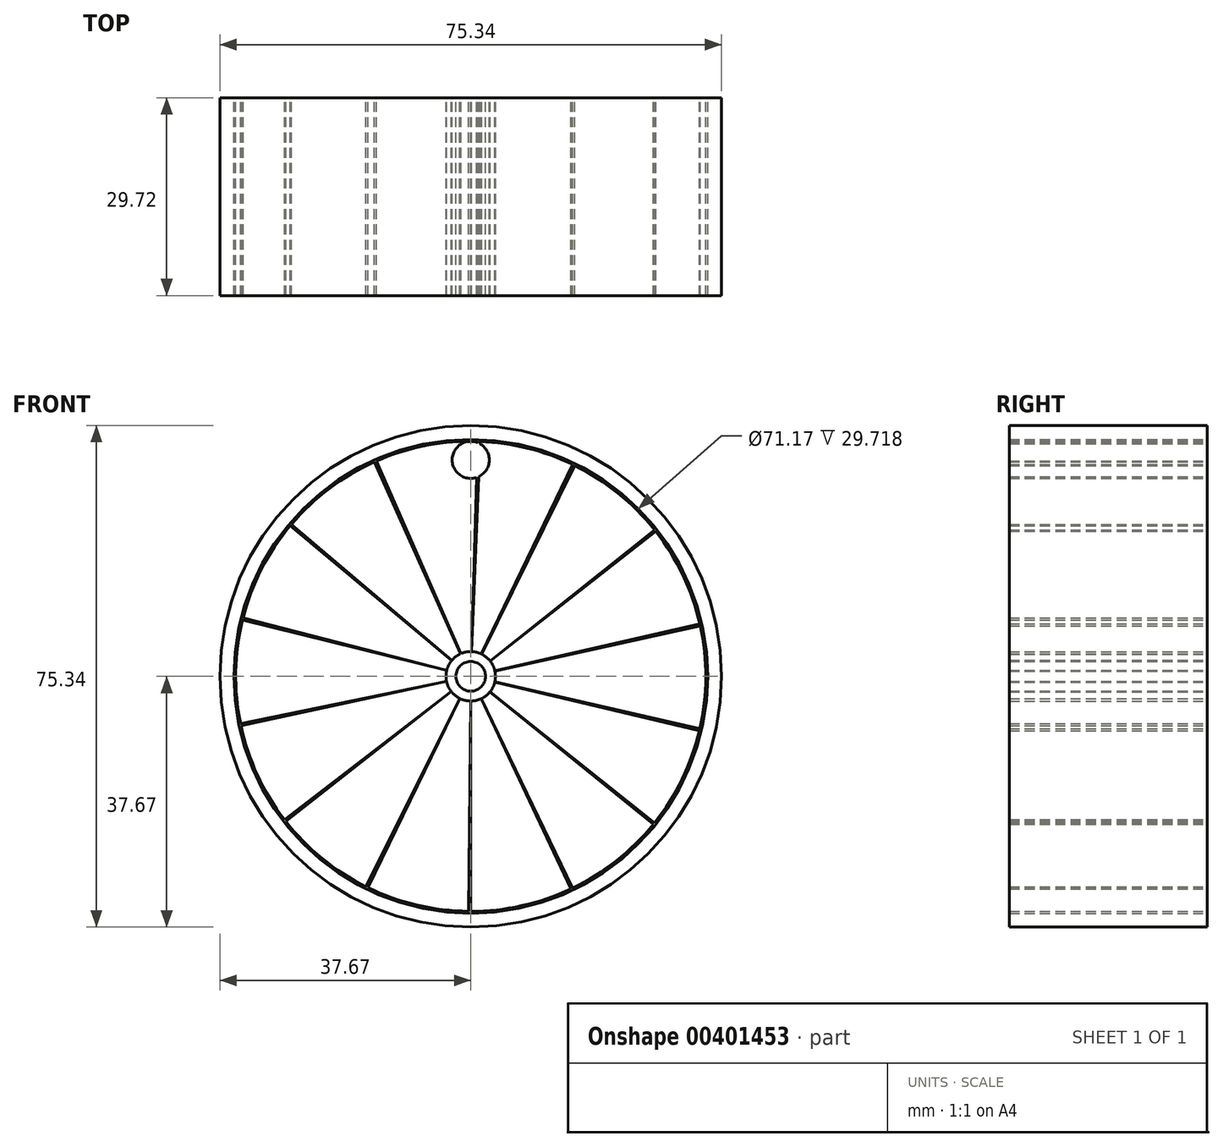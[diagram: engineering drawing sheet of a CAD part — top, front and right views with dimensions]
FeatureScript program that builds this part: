
annotation { "Feature Type Name" : "Feature", "Feature Type Description" : "" }
export const myFeature = defineFeature(function(context is Context, id is Id, definition is map)
    precondition{}
    {
        {
            var Q0;
            Q0=qCreatedBy(makeId("Front.planeOp"),FACE);
            var sketch = newSketch(context, id + "F0", { "sketchPlane" : qUnion([Q0])});
            skLineSegment(sketch, "E0", {"start": v(-30.16, 0) * mm, "end": v(30.16, 0) * mm, "construction": true});
            skCircle(sketch, "E1", {"center": v(0, 0) * mm, "radius": 30.16 * mm});
            skPoint(sketch, "E2.middle", {"position": v(0, 30.16) * mm});
            skCircle(sketch, "E3", {"center": v(0, 0) * mm, "radius": 1.9 * mm});
            skCircle(sketch, "E4", {"center": v(0, 0) * mm, "radius": 3.18 * mm});
            skCircle(sketch, "E5.0", {"center": v(0, 0) * mm, "radius": 2.54 * mm, "construction": true});
            skLineSegment(sketch, "E6.1.0", {"start": v(13.09, 27.18) * mm, "end": v(1.1, 2.29) * mm});
            skLineSegment(sketch, "E6.2.0", {"start": v(23.58, 18.8) * mm, "end": v(1.99, 1.58) * mm});
            skLineSegment(sketch, "E6.3.0", {"start": v(29.4, 6.71) * mm, "end": v(2.48, 0.57) * mm});
            skLineSegment(sketch, "E6.4.0", {"start": v(29.4, -6.71) * mm, "end": v(2.48, -0.57) * mm});
            skLineSegment(sketch, "E6.5.0", {"start": v(23.58, -18.8) * mm, "end": v(1.99, -1.58) * mm});
            skLineSegment(sketch, "E6.6.0", {"start": v(13.09, -27.18) * mm, "end": v(1.1, -2.29) * mm});
            skLineSegment(sketch, "E6.7.0", {"start": v(0, -30.16) * mm, "end": v(0, -2.54) * mm});
            skLineSegment(sketch, "E6.anchor1", {"start": v(0, 0) * mm, "end": v(0, 2.54) * mm, "construction": true});
            skLineSegment(sketch, "E6.anchor2", {"start": v(0, 0) * mm, "end": v(0, -2.54) * mm, "construction": true});
            skLineSegment(sketch, "E7.1.0", {"start": v(-13.2, -27.12) * mm, "end": v(-1.11, -2.28) * mm});
            skLineSegment(sketch, "E7.2.0", {"start": v(-23.75, -18.6) * mm, "end": v(-2, -1.57) * mm});
            skLineSegment(sketch, "E7.3.0", {"start": v(-29.5, -6.33) * mm, "end": v(-2.48, -0.53) * mm});
            skLineSegment(sketch, "E7.4.0", {"start": v(-29.28, 7.22) * mm, "end": v(-2.47, 0.6) * mm});
            skLineSegment(sketch, "E7.5.0", {"start": v(-23.17, 19.32) * mm, "end": v(-1.95, 1.63) * mm});
            skLineSegment(sketch, "E7.6.0", {"start": v(-12.37, 27.5) * mm, "end": v(-1.04, 2.32) * mm});
            skLineSegment(sketch, "E7.7.0", {"start": v(0.92, 30.15) * mm, "end": v(0.08, 2.54) * mm});
            skLineSegment(sketch, "E8.1.0", {"start": v(1.18, 30.14) * mm, "end": v(0.1, 2.54) * mm});
            skLineSegment(sketch, "E8.1.1", {"start": v(13.32, 27.06) * mm, "end": v(1.12, 2.28) * mm});
            skLineSegment(sketch, "E8.1.2", {"start": v(23.75, 18.6) * mm, "end": v(2, 1.57) * mm});
            skLineSegment(sketch, "E8.1.3", {"start": v(29.46, 6.45) * mm, "end": v(2.48, 0.54) * mm});
            skLineSegment(sketch, "E8.1.4", {"start": v(29.35, -6.97) * mm, "end": v(2.47, -0.59) * mm});
            skLineSegment(sketch, "E8.1.5", {"start": v(23.42, -19.01) * mm, "end": v(1.97, -1.6) * mm});
            skLineSegment(sketch, "E8.1.6", {"start": v(12.85, -27.29) * mm, "end": v(1.08, -2.3) * mm});
            skLineSegment(sketch, "E8.1.7", {"start": v(-0.26, -30.16) * mm, "end": v(-0.02, -2.54) * mm});
            skLineSegment(sketch, "E8.1.8", {"start": v(-13.44, -27) * mm, "end": v(-1.13, -2.27) * mm});
            skLineSegment(sketch, "E8.1.9", {"start": v(-29.55, -6.07) * mm, "end": v(-2.49, -0.51) * mm});
            skLineSegment(sketch, "E8.1.10", {"start": v(-29.22, 7.48) * mm, "end": v(-2.46, 0.63) * mm});
            skLineSegment(sketch, "E8.1.11", {"start": v(-23.9, -18.4) * mm, "end": v(-2.01, -1.55) * mm});
            skLineSegment(sketch, "E8.1.12", {"start": v(-23, 19.52) * mm, "end": v(-1.94, 1.64) * mm});
            skLineSegment(sketch, "E8.1.13", {"start": v(-12.13, 27.62) * mm, "end": v(-1.02, 2.33) * mm});
            skLineSegment(sketch, "E8.anchor1", {"start": v(0, 0) * mm, "end": v(-23.75, -18.6) * mm, "construction": true});
            skLineSegment(sketch, "E8.anchor2", {"start": v(0, 0) * mm, "end": v(-23.9, -18.4) * mm, "construction": true});
            skCircle(sketch, "E9.0", {"center": v(0, 0) * mm, "radius": 3.05 * mm});
            skCircle(sketch, "E10.0", {"center": v(0, 0) * mm, "radius": 2.03 * mm});
            skCircle(sketch, "E11.0", {"center": v(0, 0) * mm, "radius": 32.2 * mm});
            skCircle(sketch, "E12.0", {"center": v(0, 0) * mm, "radius": 30.42 * mm});
            skCircle(sketch, "E13", {"center": v(0, 27.78) * mm, "radius": 2.38 * mm});
            skSolve(sketch);
        }
        {
            var Q0;
            Q0=makeQuery(id+"F0.imprint","IMPRINT",FACE,{"disambiguationData":[TD([[makeQuery(id+"F0.imprint","IMPRINT",EDGE,{"derivedFrom":sQuery(id+"F0.wireOp",EDGE,"E11.0")}),1.0]])]});
            var Q1;
            {var subQ0=sQuery(id+"F0.wireOp",EDGE,"E6.2.0");var subQ1=sQuery(id+"F0.wireOp",EDGE,"E1");var subQ2=makeQuery(id+"F0.imprint","INTERSECT",VERTEX,{"derivedFrom":[subQ1,subQ0]});Q1=makeQuery(id+"F0.imprint","IMPRINT",FACE,{"disambiguationData":[TD([[makeQuery(id+"F0.imprint","IMPRINT",EDGE,{"disambiguationData":[TD([[subQ2,-1.0]])],"derivedFrom":subQ1}),1.0]])]});}
            var Q2;
            {var subQ0=sQuery(id+"F0.wireOp",EDGE,"E6.3.0");var subQ1=sQuery(id+"F0.wireOp",EDGE,"E1");var subQ2=makeQuery(id+"F0.imprint","INTERSECT",VERTEX,{"derivedFrom":[subQ1,subQ0]});Q2=makeQuery(id+"F0.imprint","IMPRINT",FACE,{"disambiguationData":[TD([[makeQuery(id+"F0.imprint","IMPRINT",EDGE,{"disambiguationData":[TD([[subQ2,-1.0]])],"derivedFrom":subQ1}),1.0]])]});}
            var Q3;
            {var subQ0=sQuery(id+"F0.wireOp",EDGE,"E6.4.0");var subQ1=sQuery(id+"F0.wireOp",EDGE,"E1");var subQ2=makeQuery(id+"F0.imprint","INTERSECT",VERTEX,{"derivedFrom":[subQ1,subQ0]});Q3=makeQuery(id+"F0.imprint","IMPRINT",FACE,{"disambiguationData":[TD([[makeQuery(id+"F0.imprint","IMPRINT",EDGE,{"disambiguationData":[TD([[subQ2,-1.0]])],"derivedFrom":subQ1}),1.0]])]});}
            var Q4;
            {var subQ0=sQuery(id+"F0.wireOp",EDGE,"E6.6.0");var subQ1=sQuery(id+"F0.wireOp",EDGE,"E1");var subQ2=makeQuery(id+"F0.imprint","INTERSECT",VERTEX,{"derivedFrom":[subQ1,subQ0]});Q4=makeQuery(id+"F0.imprint","IMPRINT",FACE,{"disambiguationData":[TD([[makeQuery(id+"F0.imprint","IMPRINT",EDGE,{"disambiguationData":[TD([[subQ2,-1.0]])],"derivedFrom":subQ1}),1.0]])]});}
            var Q5;
            {var subQ0=sQuery(id+"F0.wireOp",EDGE,"E6.7.0");var subQ1=sQuery(id+"F0.wireOp",EDGE,"E1");var subQ2=makeQuery(id+"F0.imprint","INTERSECT",VERTEX,{"derivedFrom":[subQ1,subQ0]});Q5=makeQuery(id+"F0.imprint","IMPRINT",FACE,{"disambiguationData":[TD([[makeQuery(id+"F0.imprint","IMPRINT",EDGE,{"disambiguationData":[TD([[subQ2,-1.0]])],"derivedFrom":subQ1}),1.0]])]});}
            var Q6;
            {var subQ0=sQuery(id+"F0.wireOp",EDGE,"E7.1.0");var subQ1=sQuery(id+"F0.wireOp",EDGE,"E1");var subQ2=makeQuery(id+"F0.imprint","INTERSECT",VERTEX,{"derivedFrom":[subQ1,subQ0]});Q6=makeQuery(id+"F0.imprint","IMPRINT",FACE,{"disambiguationData":[TD([[makeQuery(id+"F0.imprint","IMPRINT",EDGE,{"disambiguationData":[TD([[subQ2,-1.0]])],"derivedFrom":subQ1}),1.0]])]});}
            var Q7;
            {var subQ0=sQuery(id+"F0.wireOp",EDGE,"E7.2.0");var subQ1=sQuery(id+"F0.wireOp",EDGE,"E1");var subQ2=makeQuery(id+"F0.imprint","INTERSECT",VERTEX,{"derivedFrom":[subQ1,subQ0]});Q7=makeQuery(id+"F0.imprint","IMPRINT",FACE,{"disambiguationData":[TD([[makeQuery(id+"F0.imprint","IMPRINT",EDGE,{"disambiguationData":[TD([[subQ2,-1.0]])],"derivedFrom":subQ1}),1.0]])]});}
            var Q8;
            {var subQ0=sQuery(id+"F0.wireOp",EDGE,"E7.3.0");var subQ1=sQuery(id+"F0.wireOp",EDGE,"E1");var subQ2=makeQuery(id+"F0.imprint","INTERSECT",VERTEX,{"derivedFrom":[subQ1,subQ0]});Q8=makeQuery(id+"F0.imprint","IMPRINT",FACE,{"disambiguationData":[TD([[makeQuery(id+"F0.imprint","IMPRINT",EDGE,{"disambiguationData":[TD([[subQ2,-1.0]])],"derivedFrom":subQ1}),1.0]])]});}
            var Q9;
            {var subQ0=sQuery(id+"F0.wireOp",EDGE,"E7.4.0");var subQ1=sQuery(id+"F0.wireOp",EDGE,"E1");var subQ2=makeQuery(id+"F0.imprint","INTERSECT",VERTEX,{"derivedFrom":[subQ1,subQ0]});Q9=makeQuery(id+"F0.imprint","IMPRINT",FACE,{"disambiguationData":[TD([[makeQuery(id+"F0.imprint","IMPRINT",EDGE,{"disambiguationData":[TD([[subQ2,-1.0]])],"derivedFrom":subQ1}),1.0]])]});}
            var Q10;
            {var subQ0=sQuery(id+"F0.wireOp",EDGE,"E7.5.0");var subQ1=sQuery(id+"F0.wireOp",EDGE,"E1");var subQ2=makeQuery(id+"F0.imprint","INTERSECT",VERTEX,{"derivedFrom":[subQ1,subQ0]});Q10=makeQuery(id+"F0.imprint","IMPRINT",FACE,{"disambiguationData":[TD([[makeQuery(id+"F0.imprint","IMPRINT",EDGE,{"disambiguationData":[TD([[subQ2,-1.0]])],"derivedFrom":subQ1}),1.0]])]});}
            var Q11;
            {var subQ0=sQuery(id+"F0.wireOp",EDGE,"E7.6.0");var subQ1=sQuery(id+"F0.wireOp",EDGE,"E1");var subQ2=makeQuery(id+"F0.imprint","INTERSECT",VERTEX,{"derivedFrom":[subQ1,subQ0]});Q11=makeQuery(id+"F0.imprint","IMPRINT",FACE,{"disambiguationData":[TD([[makeQuery(id+"F0.imprint","IMPRINT",EDGE,{"disambiguationData":[TD([[subQ2,-1.0]])],"derivedFrom":subQ1}),1.0]])]});}
            var Q12;
            {var subQ0=sQuery(id+"F0.wireOp",EDGE,"6GiW2oyC-81qB-NawX-zeeh-e9r94Wkj5VSQ");var subQ1=sQuery(id+"F0.wireOp",EDGE,"E1");var subQ2=makeQuery(id+"F0.imprint","INTERSECT",VERTEX,{"derivedFrom":[subQ1,subQ0]});Q12=makeQuery(id+"F0.imprint","IMPRINT",FACE,{"disambiguationData":[TD([[makeQuery(id+"F0.imprint","IMPRINT",EDGE,{"disambiguationData":[TD([[subQ2,-1.0]])],"derivedFrom":subQ1}),1.0]])]});}
            var Q13;
            {var subQ0=sQuery(id+"F0.wireOp",EDGE,"E6.5.0");var subQ1=sQuery(id+"F0.wireOp",EDGE,"E1");var subQ2=makeQuery(id+"F0.imprint","INTERSECT",VERTEX,{"derivedFrom":[subQ1,subQ0]});Q13=makeQuery(id+"F0.imprint","IMPRINT",FACE,{"disambiguationData":[TD([[makeQuery(id+"F0.imprint","IMPRINT",EDGE,{"disambiguationData":[TD([[subQ2,-1.0]])],"derivedFrom":subQ1}),1.0]])]});}
            var Q14;
            Q14=makeQuery(id+"F0.imprint","IMPRINT",FACE,{"disambiguationData":[TD([[makeQuery(id+"F0.imprint","IMPRINT",EDGE,{"derivedFrom":sQuery(id+"F0.wireOp",EDGE,"E3")}),1.0]])]});
            var Q15;
            {var subQ0=sQuery(id+"F0.wireOp",EDGE,"6GiW2oyC-81qB-NawX-zeeh-e9r94Wkj5VSQ");var subQ1=sQuery(id+"F0.wireOp",EDGE,"E1");var subQ2=makeQuery(id+"F0.imprint","INTERSECT",VERTEX,{"derivedFrom":[subQ1,subQ0]});Q15=makeQuery(id+"F0.imprint","IMPRINT",FACE,{"disambiguationData":[TD([[makeQuery(id+"F0.imprint","IMPRINT",EDGE,{"disambiguationData":[TD([[subQ2,1.0]])],"derivedFrom":subQ1}),1.0]])]});}
            var Q16;
            {var subQ0=sQuery(id+"F0.wireOp",EDGE,"6GiW2oyC-81qB-NawX-zeeh-e9r94Wkj5VSQ");var subQ1=sQuery(id+"F0.wireOp",EDGE,"KhpTpVi5-M7pe-35QT-CFOe-AxJQbVMAzDhG");var subQ2=makeQuery(id+"F0.imprint","INTERSECT",VERTEX,{"disambiguationData":[OD(1.0)],"derivedFrom":[subQ1,subQ0]});Q16=makeQuery(id+"F0.imprint","IMPRINT",FACE,{"disambiguationData":[TD([[makeQuery(id+"F0.imprint","IMPRINT",EDGE,{"disambiguationData":[TD([[subQ2,-1.0]])],"derivedFrom":subQ1}),-1.0]])]});}
            var Q17;
            {var subQ1=sQuery(id+"F0.wireOp",EDGE,"E1");var subQ5=sQuery(id+"F0.wireOp",EDGE,"E6.1.0");var subQ6=makeQuery(id+"F0.imprint","INTERSECT",VERTEX,{"derivedFrom":[subQ1,subQ5]});Q17=makeQuery(id+"F0.imprint","IMPRINT",FACE,{"disambiguationData":[TD([[makeQuery(id+"F0.imprint","IMPRINT",EDGE,{"disambiguationData":[TD([[subQ6,-1.0]])],"derivedFrom":subQ1}),1.0]])]});}
            var Q18;
            {var subQ0=sQuery(id+"F0.wireOp",EDGE,"E8.1.13");var subQ1=sQuery(id+"F0.wireOp",EDGE,"E1");var subQ2=makeQuery(id+"F0.imprint","INTERSECT",VERTEX,{"derivedFrom":[subQ1,subQ0]});Q18=makeQuery(id+"F0.imprint","IMPRINT",FACE,{"disambiguationData":[TD([[makeQuery(id+"F0.imprint","IMPRINT",EDGE,{"disambiguationData":[TD([[subQ2,1.0]])],"derivedFrom":subQ1}),1.0]])]});}
            extrude(context, id + "F1", {"entities" : qUnion([Q0, Q1, Q2, Q3, Q4, Q5, Q6, Q7, Q8, Q9, Q10, Q11, Q12, Q13, Q14, Q15, Q16, Q17, Q18]), "depth" : 25.4 * mm});
        }
        {
            var Q0;
            Q0=makeQuery(id+"F1.opExtrude","SWEPT_BODY",BODY,{"disambiguationData":[OSD([sQuery(id+"F0.wireOp",EDGE,"E1"),sQuery(id+"F0.wireOp",EDGE,"E4"),sQuery(id+"F0.wireOp",EDGE,"E6.3.0"),sQuery(id+"F0.wireOp",EDGE,"E8.1.2")])]});
            var Q1;
            Q1=makeQuery(id+"F1.opExtrude","SWEPT_BODY",BODY,{"disambiguationData":[OSD([sQuery(id+"F0.wireOp",EDGE,"E11.0"),sQuery(id+"F0.wireOp",EDGE,"E12.0")])]});
            var Q2;
            Q2=makeQuery(id+"F1.opExtrude","SWEPT_BODY",BODY,{"disambiguationData":[OSD([sQuery(id+"F0.wireOp",EDGE,"E1"),sQuery(id+"F0.wireOp",EDGE,"E4"),sQuery(id+"F0.wireOp",EDGE,"E6.1.0"),sQuery(id+"F0.wireOp",EDGE,"E8.1.0"),sQuery(id+"F0.wireOp",EDGE,"E13")])]});
            var Q3;
            Q3=makeQuery(id+"F1.opExtrude","SWEPT_BODY",BODY,{"disambiguationData":[OSD([sQuery(id+"F0.wireOp",EDGE,"E1"),sQuery(id+"F0.wireOp",EDGE,"E4"),sQuery(id+"F0.wireOp",EDGE,"E6.2.0"),sQuery(id+"F0.wireOp",EDGE,"E8.1.1")])]});
            var Q4;
            Q4=makeQuery(id+"F1.opExtrude","SWEPT_BODY",BODY,{"disambiguationData":[OSD([sQuery(id+"F0.wireOp",EDGE,"E1"),sQuery(id+"F0.wireOp",EDGE,"E4"),sQuery(id+"F0.wireOp",EDGE,"E7.7.0"),sQuery(id+"F0.wireOp",EDGE,"E8.1.13"),sQuery(id+"F0.wireOp",EDGE,"E13")])]});
            var Q5;
            Q5=makeQuery(id+"F1.opExtrude","SWEPT_BODY",BODY,{"disambiguationData":[OSD([sQuery(id+"F0.wireOp",EDGE,"E1"),sQuery(id+"F0.wireOp",EDGE,"E4"),sQuery(id+"F0.wireOp",EDGE,"E7.5.0"),sQuery(id+"F0.wireOp",EDGE,"E8.1.10")])]});
            var Q6;
            Q6=makeQuery(id+"F1.opExtrude","SWEPT_BODY",BODY,{"disambiguationData":[OSD([sQuery(id+"F0.wireOp",EDGE,"E1"),sQuery(id+"F0.wireOp",EDGE,"E4"),sQuery(id+"F0.wireOp",EDGE,"E7.4.0"),sQuery(id+"F0.wireOp",EDGE,"E8.1.9")])]});
            var Q7;
            Q7=makeQuery(id+"F1.opExtrude","SWEPT_BODY",BODY,{"disambiguationData":[OSD([sQuery(id+"F0.wireOp",EDGE,"E1"),sQuery(id+"F0.wireOp",EDGE,"E4"),sQuery(id+"F0.wireOp",EDGE,"E7.3.0"),sQuery(id+"F0.wireOp",EDGE,"E8.1.11")])]});
            var Q8;
            Q8=makeQuery(id+"F1.opExtrude","SWEPT_BODY",BODY,{"disambiguationData":[OSD([sQuery(id+"F0.wireOp",EDGE,"E1"),sQuery(id+"F0.wireOp",EDGE,"E4"),sQuery(id+"F0.wireOp",EDGE,"E6.6.0"),sQuery(id+"F0.wireOp",EDGE,"E8.1.5")])]});
            var Q9;
            Q9=makeQuery(id+"F1.opExtrude","SWEPT_BODY",BODY,{"disambiguationData":[OSD([sQuery(id+"F0.wireOp",EDGE,"E1"),sQuery(id+"F0.wireOp",EDGE,"E4"),sQuery(id+"F0.wireOp",EDGE,"E7.1.0"),sQuery(id+"F0.wireOp",EDGE,"E8.1.7")])]});
            var Q10;
            Q10=makeQuery(id+"F1.opExtrude","SWEPT_BODY",BODY,{"disambiguationData":[OSD([sQuery(id+"F0.wireOp",EDGE,"E1"),sQuery(id+"F0.wireOp",EDGE,"E4"),sQuery(id+"F0.wireOp",EDGE,"E6.7.0"),sQuery(id+"F0.wireOp",EDGE,"E8.1.6")])]});
            var Q11;
            Q11=makeQuery(id+"F1.opExtrude","SWEPT_BODY",BODY,{"disambiguationData":[OSD([sQuery(id+"F0.wireOp",EDGE,"E1"),sQuery(id+"F0.wireOp",EDGE,"E4"),sQuery(id+"F0.wireOp",EDGE,"E6.5.0"),sQuery(id+"F0.wireOp",EDGE,"E8.1.4")])]});
            var Q12;
            Q12=makeQuery(id+"F1.opExtrude","SWEPT_BODY",BODY,{"disambiguationData":[OSD([sQuery(id+"F0.wireOp",EDGE,"E1"),sQuery(id+"F0.wireOp",EDGE,"E4"),sQuery(id+"F0.wireOp",EDGE,"E6.4.0"),sQuery(id+"F0.wireOp",EDGE,"E8.1.3")])]});
            var Q13;
            Q13=makeQuery(id+"F1.opExtrude","SWEPT_BODY",BODY,{"disambiguationData":[OSD([sQuery(id+"F0.wireOp",EDGE,"E1"),sQuery(id+"F0.wireOp",EDGE,"E4"),sQuery(id+"F0.wireOp",EDGE,"E7.2.0"),sQuery(id+"F0.wireOp",EDGE,"E8.1.8")])]});
            var Q14;
            Q14=makeQuery(id+"F1.opExtrude","SWEPT_BODY",BODY,{"disambiguationData":[OSD([sQuery(id+"F0.wireOp",EDGE,"E1"),sQuery(id+"F0.wireOp",EDGE,"E4"),sQuery(id+"F0.wireOp",EDGE,"E7.6.0"),sQuery(id+"F0.wireOp",EDGE,"E8.1.12")])]});
            var Q15;
            Q15=makeQuery(id+"F1.opExtrude","SWEPT_BODY",BODY,{"disambiguationData":[OSD([sQuery(id+"F0.wireOp",EDGE,"E1"),sQuery(id+"F0.wireOp",EDGE,"E7.7.0"),sQuery(id+"F0.wireOp",EDGE,"E13")])]});
            var Q16;
            Q16=makeQuery(id+"F1.opExtrude","SWEPT_BODY",BODY,{"disambiguationData":[OSD([sQuery(id+"F0.wireOp",EDGE,"E3")])]});
            var Q17;
            Q17=qCreatedBy(makeId("Origin.pointOp"),VERTEX);
            transform(context, id + "F2", {"entities" : qUnion([Q0, Q1, Q2, Q3, Q4, Q5, Q6, Q7, Q8, Q9, Q10, Q11, Q12, Q13, Q14, Q15, Q16]), "transformType" : TransformType.SCALE_UNIFORMLY, "scale" : 1.17, "scalePoint" : qUnion([Q17]), "makeCopy" : false});
        }
    });
